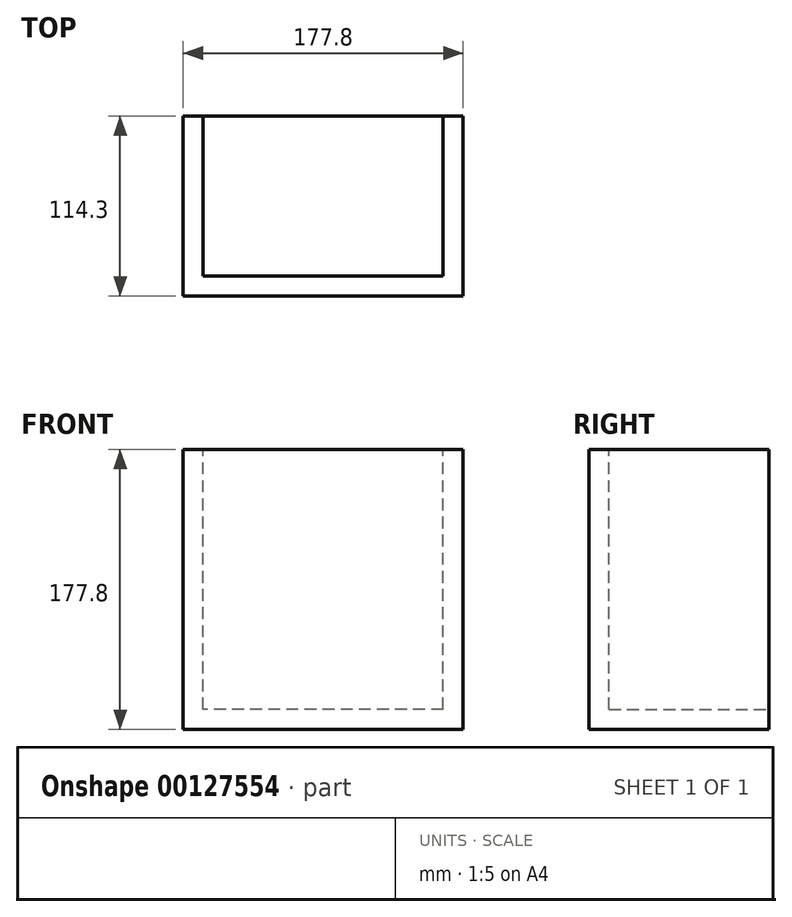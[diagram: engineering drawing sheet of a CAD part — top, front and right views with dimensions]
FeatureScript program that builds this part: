
annotation { "Feature Type Name" : "Feature", "Feature Type Description" : "" }
export const myFeature = defineFeature(function(context is Context, id is Id, definition is map)
    precondition{}
    {
        {
            var Q0;
            Q0=qCreatedBy(makeId("Front.planeOp"),FACE);
            var sketch = newSketch(context, id + "F0", { "sketchPlane" : qUnion([Q0])});
            skLineSegment(sketch, "E0.bottom", {"start": v(88.9, -88.9) * mm, "end": v(-88.9, -88.9) * mm});
            skLineSegment(sketch, "E0.top", {"start": v(88.9, 88.9) * mm, "end": v(-88.9, 88.9) * mm});
            skLineSegment(sketch, "E0.left", {"start": v(88.9, -88.9) * mm, "end": v(88.9, 88.9) * mm});
            skLineSegment(sketch, "E0.right", {"start": v(-88.9, -88.9) * mm, "end": v(-88.9, 88.9) * mm});
            skPoint(sketch, "E0.middle", {"position": v(0, 0) * mm});
            skSolve(sketch);
        }
        {
            var Q0;
            Q0 = qSketchRegion(id + "F0", true);
            extrude(context, id + "F1", {"entities" : qUnion([Q0]), "endBound" : BoundingType.SYMMETRIC, "depth" : 114.3 * mm});
        }
        {
            var Q0;
            Q0=makeQuery(id+"F1.opExtrude","SWEPT_FACE",FACE,{"disambiguationData":[OSD([sQuery(id+"F0.wireOp",EDGE,"E0.top")])]});
            var Q1;
            Q1=makeQuery(id+"F1.opExtrude","CAP_FACE",FACE,{"disambiguationData":[OSD([sQuery(id+"F0.wireOp",EDGE,"E0.bottom"),sQuery(id+"F0.wireOp",EDGE,"E0.top"),sQuery(id+"F0.wireOp",EDGE,"E0.left"),sQuery(id+"F0.wireOp",EDGE,"E0.right")])],"isStart":true});
            shell(context, id + "F2", {"entities" : qUnion([Q0, Q1]), "thickness" : 12.7 * mm});
        }
    });
